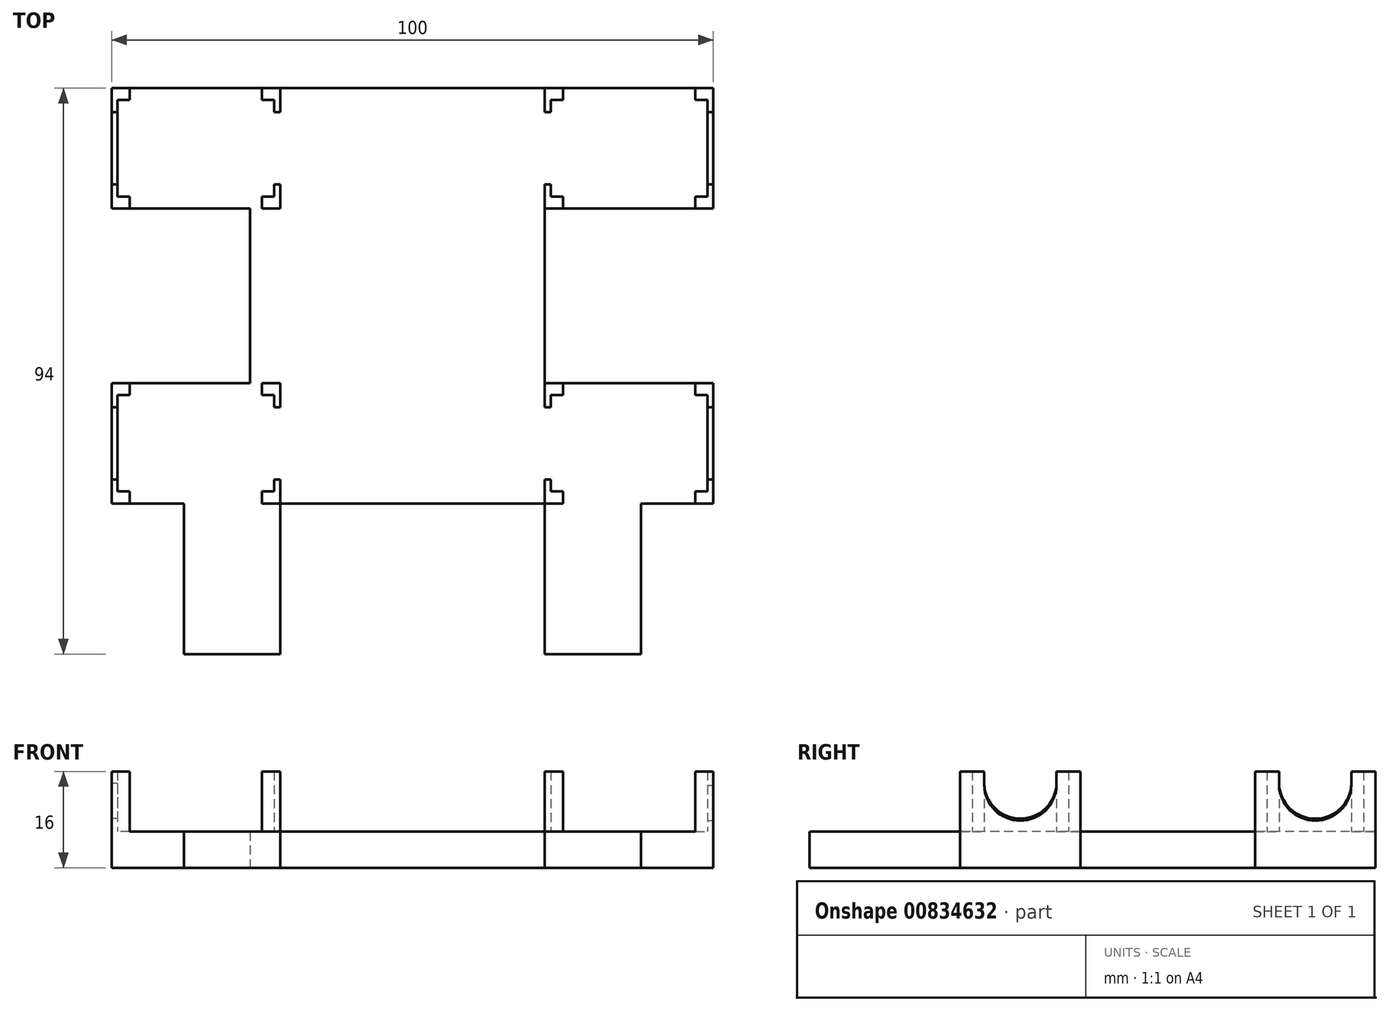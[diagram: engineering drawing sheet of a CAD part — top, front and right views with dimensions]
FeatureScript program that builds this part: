
annotation { "Feature Type Name" : "Feature", "Feature Type Description" : "" }
export const myFeature = defineFeature(function(context is Context, id is Id, definition is map)
    precondition{}
    {
        {
            var Q0;
            Q0=qCreatedBy(makeId("Top.planeOp"),FACE);
            var sketch = newSketch(context, id + "F0", { "sketchPlane" : qUnion([Q0])});
            skLineSegment(sketch, "E0.bottom", {"start": v(-60, -33.28) * mm, "end": v(-44, -33.28) * mm});
            skLineSegment(sketch, "E0.top", {"start": v(-72, 60.72) * mm, "end": v(28, 60.72) * mm});
            skLineSegment(sketch, "E0.right", {"start": v(28, -8.28) * mm, "end": v(28, 11.72) * mm});
            skLineSegment(sketch, "E1.right", {"start": v(-60, -8.28) * mm, "end": v(-60, -33.28) * mm});
            skLineSegment(sketch, "E2.top", {"start": v(-44, -8.28) * mm, "end": v(0, -8.28) * mm});
            skLineSegment(sketch, "E2.left", {"start": v(-44, -33.28) * mm, "end": v(-44, -8.28) * mm});
            skLineSegment(sketch, "E2.right", {"start": v(0, -33.28) * mm, "end": v(0, -8.28) * mm});
            skLineSegment(sketch, "E3.top", {"start": v(16, -8.28) * mm, "end": v(28, -8.28) * mm});
            skLineSegment(sketch, "E3.left", {"start": v(16, -33.28) * mm, "end": v(16, -8.28) * mm});
            skLineSegment(sketch, "E4.top", {"start": v(-72, 40.72) * mm, "end": v(-49, 40.72) * mm});
            skLineSegment(sketch, "E4.right", {"start": v(-49, 11.72) * mm, "end": v(-49, 40.72) * mm});
            skLineSegment(sketch, "E5.bottom", {"start": v(28, 40.72) * mm, "end": v(0, 40.72) * mm});
            skLineSegment(sketch, "E5.top", {"start": v(28, 11.72) * mm, "end": v(0, 11.72) * mm});
            skLineSegment(sketch, "E5.right", {"start": v(0, 40.72) * mm, "end": v(0, 11.72) * mm});
            skLineSegment(sketch, "E6.trimOffspring", {"start": v(28, 40.72) * mm, "end": v(28, 60.72) * mm});
            skLineSegment(sketch, "E7.trimOffspring", {"start": v(0, -33.28) * mm, "end": v(16, -33.28) * mm});
            skLineSegment(sketch, "E8", {"start": v(-72, -8.28) * mm, "end": v(-60, -8.28) * mm});
            skLineSegment(sketch, "E9.left", {"start": v(-72, -8.28) * mm, "end": v(-72, -4.28) * mm});
            skLineSegment(sketch, "E10", {"start": v(-72, -8.28) * mm, "end": v(-69, -8.28) * mm});
            skLineSegment(sketch, "E11", {"start": v(-72, -8.28) * mm, "end": v(-72, 11.74) * mm});
            skLineSegment(sketch, "E12", {"start": v(-72, 11.74) * mm, "end": v(-49, 11.72) * mm});
            skLineSegment(sketch, "E13", {"start": v(-72, 11.7) * mm, "end": v(-69, 11.7) * mm});
            skLineSegment(sketch, "E14.MirrorCS", {"start": v(-72, 11.7) * mm, "end": v(-72, 7.7) * mm});
            skLineSegment(sketch, "E15", {"start": v(-72, 60.72) * mm, "end": v(-72, 40.72) * mm});
            skSolve(sketch);
        }
        {
            var Q0;
            Q0=makeQuery(id+"F0.imprint","IMPRINT",FACE,{"disambiguationData":[TD([[makeQuery(id+"F0.imprint","IMPRINT",EDGE,{"derivedFrom":sQuery(id+"F0.wireOp",EDGE,"E0.bottom")}),1.0]])]});
            extrude(context, id + "F1", {"entities" : qUnion([Q0]), "depth" : 6 * mm, "offsetDistance" : 25 * mm});
        }
        {
            var Q0;
            Q0=makeQuery(id+"F1.opExtrude","CAP_FACE",FACE,{"disambiguationData":[OSD([sQuery(id+"F0.wireOp",EDGE,"E0.bottom"),sQuery(id+"F0.wireOp",EDGE,"E0.top"),sQuery(id+"F0.wireOp",EDGE,"E0.right"),sQuery(id+"F0.wireOp",EDGE,"E1.right"),sQuery(id+"F0.wireOp",EDGE,"E2.top"),sQuery(id+"F0.wireOp",EDGE,"E2.left"),sQuery(id+"F0.wireOp",EDGE,"E2.right"),sQuery(id+"F0.wireOp",EDGE,"E3.top"),sQuery(id+"F0.wireOp",EDGE,"E3.left"),sQuery(id+"F0.wireOp",EDGE,"E4.top"),sQuery(id+"F0.wireOp",EDGE,"E4.right"),sQuery(id+"F0.wireOp",EDGE,"E5.bottom"),sQuery(id+"F0.wireOp",EDGE,"E5.top"),sQuery(id+"F0.wireOp",EDGE,"E5.right"),sQuery(id+"F0.wireOp",EDGE,"E6.trimOffspring"),sQuery(id+"F0.wireOp",EDGE,"E7.trimOffspring"),sQuery(id+"F0.wireOp",EDGE,"E8"),sQuery(id+"F0.wireOp",EDGE,"E10"),sQuery(id+"F0.wireOp",EDGE,"E11"),sQuery(id+"F0.wireOp",EDGE,"E12"),sQuery(id+"F0.wireOp",EDGE,"E14.MirrorCS"),sQuery(id+"F0.wireOp",EDGE,"E15")])],"isStart":false});
            var sketch = newSketch(context, id + "F2", { "sketchPlane" : qUnion([Q0])});
            skLineSegment(sketch, "E16", {"start": v(-72, -8.28) * mm, "end": v(-69, -8.28) * mm});
            skLineSegment(sketch, "E17", {"start": v(-69, -8.28) * mm, "end": v(-69, -6.28) * mm});
            skLineSegment(sketch, "E18", {"start": v(-69, -6.28) * mm, "end": v(-71, -6.28) * mm});
            skLineSegment(sketch, "E19", {"start": v(-71, -6.28) * mm, "end": v(-71, -4.28) * mm});
            skLineSegment(sketch, "E20", {"start": v(-71, -4.28) * mm, "end": v(-72, -4.28) * mm});
            skLineSegment(sketch, "E21", {"start": v(-72, -4.28) * mm, "end": v(-72, -8.28) * mm});
            skLineSegment(sketch, "E22", {"start": v(-72, 1.73) * mm, "end": v(28, 1.73) * mm, "construction": true});
            skLineSegment(sketch, "E23", {"start": v(28, 40.72) * mm, "end": v(28, 11.72) * mm, "construction": true});
            skLineSegment(sketch, "E24", {"start": v(-72, 40.72) * mm, "end": v(-72, 11.74) * mm, "construction": true});
            skLineSegment(sketch, "E25", {"start": v(-22, -8.28) * mm, "end": v(-22, 60.72) * mm, "construction": true});
            skLineSegment(sketch, "E26", {"start": v(-72, 26.23) * mm, "end": v(28, 26.23) * mm, "construction": true});
            skLineSegment(sketch, "E27.MirrorCS", {"start": v(-71, 7.74) * mm, "end": v(-72, 7.74) * mm});
            skLineSegment(sketch, "E28.MirrorCS", {"start": v(-69, 9.74) * mm, "end": v(-71, 9.74) * mm});
            skLineSegment(sketch, "E29.MirrorCS", {"start": v(-69, 11.74) * mm, "end": v(-69, 9.74) * mm});
            skLineSegment(sketch, "E30.MirrorCS", {"start": v(-71, 9.74) * mm, "end": v(-71, 7.74) * mm});
            skLineSegment(sketch, "E31.MirrorCS", {"start": v(-72, 7.74) * mm, "end": v(-72, 11.74) * mm});
            skLineSegment(sketch, "E32.MirrorCS", {"start": v(-72, 11.74) * mm, "end": v(-69, 11.74) * mm});
            skLineSegment(sketch, "E33", {"start": v(-72, 1.73) * mm, "end": v(-57.98, 1.73) * mm});
            skLineSegment(sketch, "E34", {"start": v(-72, 16.41) * mm, "end": v(-58, 16.41) * mm, "construction": true});
            skLineSegment(sketch, "E35", {"start": v(-58, 16.41) * mm, "end": v(-58, -8.8) * mm, "construction": true});
            skLineSegment(sketch, "E36.MirrorCS", {"start": v(-44, 7.74) * mm, "end": v(-44, 11.74) * mm});
            skLineSegment(sketch, "E37.MirrorCS", {"start": v(-45, -4.28) * mm, "end": v(-44, -4.28) * mm});
            skLineSegment(sketch, "E38.MirrorCS", {"start": v(-47, 11.74) * mm, "end": v(-47, 9.74) * mm});
            skLineSegment(sketch, "E39.MirrorCS", {"start": v(-45, 7.74) * mm, "end": v(-44, 7.74) * mm});
            skLineSegment(sketch, "E40.MirrorCS", {"start": v(-47, -6.28) * mm, "end": v(-45, -6.28) * mm});
            skLineSegment(sketch, "E41.MirrorCS", {"start": v(-47, -8.28) * mm, "end": v(-47, -6.28) * mm});
            skLineSegment(sketch, "E42.MirrorCS", {"start": v(-45, -6.28) * mm, "end": v(-45, -4.28) * mm});
            skLineSegment(sketch, "E43.MirrorCS", {"start": v(-47, 9.74) * mm, "end": v(-45, 9.74) * mm});
            skLineSegment(sketch, "E44.MirrorCS", {"start": v(-45, 9.74) * mm, "end": v(-45, 7.74) * mm});
            skLineSegment(sketch, "E45.MirrorCS", {"start": v(-44, -8.28) * mm, "end": v(-47, -8.28) * mm});
            skLineSegment(sketch, "E46.MirrorCS", {"start": v(-44, -4.28) * mm, "end": v(-44, -8.28) * mm});
            skLineSegment(sketch, "E47.MirrorCS", {"start": v(-44, 11.74) * mm, "end": v(-47, 11.74) * mm});
            skLineSegment(sketch, "E48.MirrorCS", {"start": v(27, 7.74) * mm, "end": v(28, 7.74) * mm});
            skLineSegment(sketch, "E49.MirrorCS", {"start": v(27, 9.74) * mm, "end": v(27, 7.74) * mm});
            skLineSegment(sketch, "E50.MirrorCS", {"start": v(28, 7.74) * mm, "end": v(28, 11.74) * mm});
            skLineSegment(sketch, "E51.MirrorCS", {"start": v(25, 11.74) * mm, "end": v(25, 9.74) * mm});
            skLineSegment(sketch, "E52.MirrorCS", {"start": v(1, 9.74) * mm, "end": v(1, 7.74) * mm});
            skLineSegment(sketch, "E53.MirrorCS", {"start": v(25, 9.74) * mm, "end": v(27, 9.74) * mm});
            skLineSegment(sketch, "E54.MirrorCS", {"start": v(3, -6.28) * mm, "end": v(1, -6.28) * mm});
            skLineSegment(sketch, "E55.MirrorCS", {"start": v(3, 9.74) * mm, "end": v(1, 9.74) * mm});
            skLineSegment(sketch, "E56.MirrorCS", {"start": v(1, -6.28) * mm, "end": v(1, -4.28) * mm});
            skLineSegment(sketch, "E57.MirrorCS", {"start": v(3, -8.28) * mm, "end": v(3, -6.28) * mm});
            skLineSegment(sketch, "E58.MirrorCS", {"start": v(1, 7.74) * mm, "end": v(0, 7.74) * mm});
            skLineSegment(sketch, "E59.MirrorCS", {"start": v(25, -8.28) * mm, "end": v(25, -6.28) * mm});
            skLineSegment(sketch, "E60.MirrorCS", {"start": v(25, -6.28) * mm, "end": v(27, -6.28) * mm});
            skLineSegment(sketch, "E61.MirrorCS", {"start": v(27, -6.28) * mm, "end": v(27, -4.28) * mm});
            skLineSegment(sketch, "E62.MirrorCS", {"start": v(0, 7.74) * mm, "end": v(0, 11.74) * mm});
            skLineSegment(sketch, "E63.MirrorCS", {"start": v(27, -4.28) * mm, "end": v(28, -4.28) * mm});
            skLineSegment(sketch, "E64.MirrorCS", {"start": v(3, 11.74) * mm, "end": v(3, 9.74) * mm});
            skLineSegment(sketch, "E65.MirrorCS", {"start": v(1, -4.28) * mm, "end": v(0, -4.28) * mm});
            skLineSegment(sketch, "E66.MirrorCS", {"start": v(28, -8.28) * mm, "end": v(25, -8.28) * mm});
            skLineSegment(sketch, "E67.MirrorCS", {"start": v(28, -4.28) * mm, "end": v(28, -8.28) * mm});
            skLineSegment(sketch, "E68.MirrorCS", {"start": v(0, 11.74) * mm, "end": v(3, 11.74) * mm});
            skLineSegment(sketch, "E69.MirrorCS", {"start": v(0, -4.28) * mm, "end": v(0, -8.28) * mm});
            skLineSegment(sketch, "E70.MirrorCS", {"start": v(0, -8.28) * mm, "end": v(3, -8.28) * mm});
            skLineSegment(sketch, "E71.MirrorCS", {"start": v(28, 11.74) * mm, "end": v(25, 11.74) * mm});
            skLineSegment(sketch, "E72.MirrorCS", {"start": v(28, 1.73) * mm, "end": v(13.98, 1.73) * mm});
            skLineSegment(sketch, "E73.MirrorCS", {"start": v(28, 56.74) * mm, "end": v(28, 60.74) * mm});
            skLineSegment(sketch, "E74.MirrorCS", {"start": v(-71, 58.74) * mm, "end": v(-71, 56.74) * mm});
            skLineSegment(sketch, "E75.MirrorCS", {"start": v(-47, 58.74) * mm, "end": v(-45, 58.74) * mm});
            skLineSegment(sketch, "E76.MirrorCS", {"start": v(-69, 42.72) * mm, "end": v(-71, 42.72) * mm});
            skLineSegment(sketch, "E77.MirrorCS", {"start": v(25, 58.74) * mm, "end": v(27, 58.74) * mm});
            skLineSegment(sketch, "E78.MirrorCS", {"start": v(-47, 42.72) * mm, "end": v(-45, 42.72) * mm});
            skLineSegment(sketch, "E79.MirrorCS", {"start": v(-72, 44.72) * mm, "end": v(-72, 40.72) * mm});
            skLineSegment(sketch, "E80.MirrorCS", {"start": v(27, 58.74) * mm, "end": v(27, 56.74) * mm});
            skLineSegment(sketch, "E81.MirrorCS", {"start": v(-71, 42.72) * mm, "end": v(-71, 44.72) * mm});
            skLineSegment(sketch, "E82.MirrorCS", {"start": v(-45, 58.74) * mm, "end": v(-45, 56.74) * mm});
            skLineSegment(sketch, "E83.MirrorCS", {"start": v(-45, 42.72) * mm, "end": v(-45, 44.72) * mm});
            skLineSegment(sketch, "E84.MirrorCS", {"start": v(-44, 56.74) * mm, "end": v(-44, 60.74) * mm});
            skLineSegment(sketch, "E85.MirrorCS", {"start": v(-69, 58.74) * mm, "end": v(-71, 58.74) * mm});
            skLineSegment(sketch, "E86.MirrorCS", {"start": v(-72, 40.72) * mm, "end": v(-69, 40.72) * mm});
            skLineSegment(sketch, "E87.MirrorCS", {"start": v(27, 44.72) * mm, "end": v(28, 44.72) * mm});
            skLineSegment(sketch, "E88.MirrorCS", {"start": v(3, 40.72) * mm, "end": v(3, 42.72) * mm});
            skLineSegment(sketch, "E89.MirrorCS", {"start": v(27, 42.72) * mm, "end": v(27, 44.72) * mm});
            skLineSegment(sketch, "E90.MirrorCS", {"start": v(1, 56.74) * mm, "end": v(0, 56.74) * mm});
            skLineSegment(sketch, "E91.MirrorCS", {"start": v(-72, 56.74) * mm, "end": v(-72, 60.74) * mm});
            skLineSegment(sketch, "E92.MirrorCS", {"start": v(28, 44.72) * mm, "end": v(28, 40.72) * mm});
            skLineSegment(sketch, "E93.MirrorCS", {"start": v(28, 60.74) * mm, "end": v(25, 60.74) * mm});
            skLineSegment(sketch, "E94.MirrorCS", {"start": v(-71, 56.74) * mm, "end": v(-72, 56.74) * mm});
            skLineSegment(sketch, "E95.MirrorCS", {"start": v(25, 40.72) * mm, "end": v(25, 42.72) * mm});
            skLineSegment(sketch, "E96.MirrorCS", {"start": v(-44, 40.72) * mm, "end": v(-47, 40.72) * mm});
            skLineSegment(sketch, "E97.MirrorCS", {"start": v(27, 56.74) * mm, "end": v(28, 56.74) * mm});
            skLineSegment(sketch, "E98.MirrorCS", {"start": v(-44, 44.72) * mm, "end": v(-44, 40.72) * mm});
            skLineSegment(sketch, "E99.MirrorCS", {"start": v(-44, 60.74) * mm, "end": v(-47, 60.74) * mm});
            skLineSegment(sketch, "E100.MirrorCS", {"start": v(3, 42.72) * mm, "end": v(1, 42.72) * mm});
            skLineSegment(sketch, "E101.MirrorCS", {"start": v(3, 58.74) * mm, "end": v(1, 58.74) * mm});
            skLineSegment(sketch, "E102.MirrorCS", {"start": v(3, 60.74) * mm, "end": v(3, 58.74) * mm});
            skLineSegment(sketch, "E103.MirrorCS", {"start": v(28, 40.72) * mm, "end": v(25, 40.72) * mm});
            skLineSegment(sketch, "E104.MirrorCS", {"start": v(-69, 60.74) * mm, "end": v(-69, 58.74) * mm});
            skLineSegment(sketch, "E105.MirrorCS", {"start": v(0, 60.74) * mm, "end": v(3, 60.74) * mm});
            skLineSegment(sketch, "E106.MirrorCS", {"start": v(-71, 44.72) * mm, "end": v(-72, 44.72) * mm});
            skLineSegment(sketch, "E107.MirrorCS", {"start": v(-45, 56.74) * mm, "end": v(-44, 56.74) * mm});
            skLineSegment(sketch, "E108.MirrorCS", {"start": v(1, 44.72) * mm, "end": v(0, 44.72) * mm});
            skLineSegment(sketch, "E109.MirrorCS", {"start": v(-47, 60.74) * mm, "end": v(-47, 58.74) * mm});
            skLineSegment(sketch, "E110.MirrorCS", {"start": v(0, 56.74) * mm, "end": v(0, 60.74) * mm});
            skLineSegment(sketch, "E111.MirrorCS", {"start": v(0, 40.72) * mm, "end": v(3, 40.72) * mm});
            skLineSegment(sketch, "E112.MirrorCS", {"start": v(0, 44.72) * mm, "end": v(0, 40.72) * mm});
            skLineSegment(sketch, "E113.MirrorCS", {"start": v(-47, 40.72) * mm, "end": v(-47, 42.72) * mm});
            skLineSegment(sketch, "E114.MirrorCS", {"start": v(1, 42.72) * mm, "end": v(1, 44.72) * mm});
            skLineSegment(sketch, "E115.MirrorCS", {"start": v(25, 60.74) * mm, "end": v(25, 58.74) * mm});
            skLineSegment(sketch, "E116.MirrorCS", {"start": v(25, 42.72) * mm, "end": v(27, 42.72) * mm});
            skLineSegment(sketch, "E117.MirrorCS", {"start": v(-72, 60.74) * mm, "end": v(-69, 60.74) * mm});
            skLineSegment(sketch, "E118.MirrorCS", {"start": v(-45, 44.72) * mm, "end": v(-44, 44.72) * mm});
            skLineSegment(sketch, "E119.MirrorCS", {"start": v(-69, 40.72) * mm, "end": v(-69, 42.72) * mm});
            skLineSegment(sketch, "E120.MirrorCS", {"start": v(1, 58.74) * mm, "end": v(1, 56.74) * mm});
            skLineSegment(sketch, "E121.MirrorCS", {"start": v(-72, 50.73) * mm, "end": v(-57.98, 50.73) * mm});
            skLineSegment(sketch, "E122.MirrorCS", {"start": v(28, 50.73) * mm, "end": v(13.98, 50.73) * mm});
            skLineSegment(sketch, "E123.MirrorCS", {"start": v(-72, 50.73) * mm, "end": v(28, 50.73) * mm, "construction": true});
            skSolve(sketch);
        }
        {
            var Q0;
            Q0=makeQuery(id+"F2.imprint","IMPRINT",FACE,{"disambiguationData":[TD([[makeQuery(id+"F2.imprint","IMPRINT",EDGE,{"derivedFrom":sQuery(id+"F2.wireOp",EDGE,"E74.MirrorCS")}),-1.0]])]});
            var Q1;
            Q1=makeQuery(id+"F2.imprint","IMPRINT",FACE,{"disambiguationData":[TD([[makeQuery(id+"F2.imprint","IMPRINT",EDGE,{"derivedFrom":sQuery(id+"F2.wireOp",EDGE,"E76.MirrorCS")}),1.0]])]});
            var Q2;
            Q2=makeQuery(id+"F2.imprint","IMPRINT",FACE,{"disambiguationData":[TD([[makeQuery(id+"F2.imprint","IMPRINT",EDGE,{"derivedFrom":sQuery(id+"F2.wireOp",EDGE,"E78.MirrorCS")}),-1.0]])]});
            var Q3;
            {var subQ6=sQuery(id+"F2.wireOp",EDGE,"E75.MirrorCS");Q3=makeQuery(id+"F2.imprint","IMPRINT",FACE,{"disambiguationData":[TD([[makeQuery(id+"F2.imprint","IMPRINT",EDGE,{"derivedFrom":subQ6}),1.0]])]});}
            var Q4;
            {var subQ1=sQuery(id+"F2.wireOp",EDGE,"E77.MirrorCS");Q4=makeQuery(id+"F2.imprint","IMPRINT",FACE,{"disambiguationData":[TD([[makeQuery(id+"F2.imprint","IMPRINT",EDGE,{"derivedFrom":subQ1}),1.0]])]});}
            var Q5;
            Q5=makeQuery(id+"F2.imprint","IMPRINT",FACE,{"disambiguationData":[TD([[makeQuery(id+"F2.imprint","IMPRINT",EDGE,{"derivedFrom":sQuery(id+"F2.wireOp",EDGE,"E87.MirrorCS")}),-1.0]])]});
            var Q6;
            Q6=makeQuery(id+"F2.imprint","IMPRINT",FACE,{"disambiguationData":[TD([[makeQuery(id+"F2.imprint","IMPRINT",EDGE,{"derivedFrom":sQuery(id+"F2.wireOp",EDGE,"E88.MirrorCS")}),1.0]])]});
            var Q7;
            {var subQ1=sQuery(id+"F2.wireOp",EDGE,"E90.MirrorCS");Q7=makeQuery(id+"F2.imprint","IMPRINT",FACE,{"disambiguationData":[TD([[makeQuery(id+"F2.imprint","IMPRINT",EDGE,{"derivedFrom":subQ1}),-1.0]])]});}
            var Q8;
            {var subQ3=sQuery(id+"F2.wireOp",EDGE,"E48.MirrorCS");Q8=makeQuery(id+"F2.imprint","IMPRINT",FACE,{"disambiguationData":[TD([[makeQuery(id+"F2.imprint","IMPRINT",EDGE,{"derivedFrom":subQ3}),1.0]])]});}
            var Q9;
            Q9=makeQuery(id+"F2.imprint","IMPRINT",FACE,{"disambiguationData":[TD([[makeQuery(id+"F2.imprint","IMPRINT",EDGE,{"derivedFrom":sQuery(id+"F2.wireOp",EDGE,"E59.MirrorCS")}),-1.0]])]});
            var Q10;
            Q10=makeQuery(id+"F2.imprint","IMPRINT",FACE,{"disambiguationData":[TD([[makeQuery(id+"F2.imprint","IMPRINT",EDGE,{"derivedFrom":sQuery(id+"F2.wireOp",EDGE,"E54.MirrorCS")}),1.0]])]});
            var Q11;
            Q11=makeQuery(id+"F2.imprint","IMPRINT",FACE,{"disambiguationData":[TD([[makeQuery(id+"F2.imprint","IMPRINT",EDGE,{"derivedFrom":sQuery(id+"F2.wireOp",EDGE,"E52.MirrorCS")}),-1.0]])]});
            var Q12;
            Q12=makeQuery(id+"F2.imprint","IMPRINT",FACE,{"disambiguationData":[TD([[makeQuery(id+"F2.imprint","IMPRINT",EDGE,{"derivedFrom":sQuery(id+"F2.wireOp",EDGE,"E36.MirrorCS")}),1.0]])]});
            var Q13;
            Q13=makeQuery(id+"F2.imprint","IMPRINT",FACE,{"disambiguationData":[TD([[makeQuery(id+"F2.imprint","IMPRINT",EDGE,{"derivedFrom":sQuery(id+"F2.wireOp",EDGE,"E37.MirrorCS")}),-1.0]])]});
            var Q14;
            Q14=makeQuery(id+"F2.imprint","IMPRINT",FACE,{"disambiguationData":[TD([[makeQuery(id+"F2.imprint","IMPRINT",EDGE,{"derivedFrom":sQuery(id+"F2.wireOp",EDGE,"E16")}),1.0]])]});
            var Q15;
            Q15=makeQuery(id+"F2.imprint","IMPRINT",FACE,{"disambiguationData":[TD([[makeQuery(id+"F2.imprint","IMPRINT",EDGE,{"derivedFrom":sQuery(id+"F2.wireOp",EDGE,"E27.MirrorCS")}),-1.0]])]});
            extrude(context, id + "F3", {"entities" : qUnion([Q0, Q1, Q2, Q3, Q4, Q5, Q6, Q7, Q8, Q9, Q10, Q11, Q12, Q13, Q14, Q15]), "operationType" : NewBodyOperationType.ADD, "depth" : 10 * mm, "offsetDistance" : 25 * mm});
        }
        {
            var Q0;
            Q0=makeQuery(id+"F3.boolean.opBoolean","MERGE",FACE,{"derivedFrom":[makeQuery(id+"F1.opExtrude","SWEPT_FACE",FACE,{"disambiguationData":[OSD([sQuery(id+"F0.wireOp",EDGE,"E0.right")])]}),makeQuery(id+"F3.opExtrude","SWEPT_FACE",FACE,{"disambiguationData":[OSD([sQuery(id+"F2.wireOp",EDGE,"E50.MirrorCS")])]}),makeQuery(id+"F3.opExtrude","SWEPT_FACE",FACE,{"disambiguationData":[OSD([sQuery(id+"F2.wireOp",EDGE,"E67.MirrorCS")])]})]});
            var sketch = newSketch(context, id + "F4", { "sketchPlane" : qUnion([Q0])});
            skArc(sketch, "E124", {"start": v(-4.28, 14) * mm, "mid": v(1.73, 7.82) * mm, "end": v(7.74, 14) * mm});
            skSolve(sketch);
        }
        {
            var Q0;
            {var subQ1=sQuery(id+"F0.wireOp",EDGE,"E0.right");var subQ6=makeQuery(id+"F1.opExtrude","CAP_EDGE",EDGE,{"disambiguationData":[OSD([subQ1])],"isStart":false});Q0=makeQuery(id+"F4.imprint","IMPRINT",FACE,{"disambiguationData":[TD([[makeQuery(id+"F4.imprint","IMPRINT",EDGE,{"derivedFrom":subQ6}),1.0]])]});}
            extrude(context, id + "F5", {"entities" : qUnion([Q0]), "operationType" : NewBodyOperationType.ADD, "oppositeDirection" : true, "depth" : 1 * mm, "offsetDistance" : 25 * mm});
        }
        {
            var Q0;
            Q0=makeQuery(id+"F3.boolean.opBoolean","MERGE",FACE,{"derivedFrom":[makeQuery(id+"F1.opExtrude","SWEPT_FACE",FACE,{"disambiguationData":[OSD([sQuery(id+"F0.wireOp",EDGE,"E6.trimOffspring")])]}),makeQuery(id+"F3.opExtrude","SWEPT_FACE",FACE,{"disambiguationData":[OSD([sQuery(id+"F2.wireOp",EDGE,"E73.MirrorCS")])]}),makeQuery(id+"F3.opExtrude","SWEPT_FACE",FACE,{"disambiguationData":[OSD([sQuery(id+"F2.wireOp",EDGE,"E92.MirrorCS")])]})]});
            var sketch = newSketch(context, id + "F6", { "sketchPlane" : qUnion([Q0])});
            skArc(sketch, "E125", {"start": v(44.72, 14) * mm, "mid": v(50.73, 7.82) * mm, "end": v(56.74, 14) * mm});
            skSolve(sketch);
        }
        {
            var Q0;
            {var subQ1=sQuery(id+"F0.wireOp",EDGE,"E6.trimOffspring");var subQ6=makeQuery(id+"F1.opExtrude","CAP_EDGE",EDGE,{"disambiguationData":[OSD([subQ1])],"isStart":false});Q0=makeQuery(id+"F6.imprint","IMPRINT",FACE,{"disambiguationData":[TD([[makeQuery(id+"F6.imprint","IMPRINT",EDGE,{"derivedFrom":subQ6}),1.0]])]});}
            extrude(context, id + "F7", {"entities" : qUnion([Q0]), "operationType" : NewBodyOperationType.ADD, "oppositeDirection" : true, "depth" : 1 * mm, "offsetDistance" : 25 * mm});
        }
        {
            var Q0;
            Q0=makeQuery(id+"F3.boolean.opBoolean","MERGE",FACE,{"derivedFrom":[makeQuery(id+"F1.opExtrude","SWEPT_FACE",FACE,{"disambiguationData":[OSD([sQuery(id+"F0.wireOp",EDGE,"E15")])]}),makeQuery(id+"F3.opExtrude","SWEPT_FACE",FACE,{"disambiguationData":[OSD([sQuery(id+"F2.wireOp",EDGE,"E79.MirrorCS")])]}),makeQuery(id+"F3.opExtrude","SWEPT_FACE",FACE,{"disambiguationData":[OSD([sQuery(id+"F2.wireOp",EDGE,"E91.MirrorCS")])]})]});
            var sketch = newSketch(context, id + "F8", { "sketchPlane" : qUnion([Q0])});
            skArc(sketch, "E126", {"start": v(-7.74, 14) * mm, "mid": v(-1.73, 7.82) * mm, "end": v(4.28, 14) * mm});
            skArc(sketch, "E127", {"start": v(-56.74, 14) * mm, "mid": v(-50.73, 8.14) * mm, "end": v(-44.72, 14) * mm});
            skLineSegment(sketch, "E128", {"start": v(-7.74, 14) * mm, "end": v(-7.74, 5.95) * mm});
            skLineSegment(sketch, "E129", {"start": v(-7.74, 5.95) * mm, "end": v(4.39, 5.95) * mm});
            skLineSegment(sketch, "E130", {"start": v(4.39, 5.95) * mm, "end": v(4.28, 14) * mm});
            skSolve(sketch);
        }
        {
            var Q0;
            {var subQ0=sQuery(id+"F8.wireOp",EDGE,"E127");Q0=makeQuery(id+"F8.imprint","IMPRINT",FACE,{"disambiguationData":[TD([[makeQuery(id+"F8.imprint","IMPRINT",EDGE,{"derivedFrom":subQ0}),-1.0]])]});}
            extrude(context, id + "F9", {"entities" : qUnion([Q0]), "operationType" : NewBodyOperationType.ADD, "oppositeDirection" : true, "depth" : 1 * mm, "offsetDistance" : 25 * mm});
        }
        {
            var Q0;
            {var subQ5=sQuery(id+"F8.wireOp",EDGE,"E129");Q0=makeQuery(id+"F8.imprint","IMPRINT",FACE,{"disambiguationData":[TD([[makeQuery(id+"F8.imprint","IMPRINT",EDGE,{"derivedFrom":subQ5}),1.0]])]});}
            extrude(context, id + "F10", {"entities" : qUnion([Q0]), "oppositeDirection" : true, "depth" : 1 * mm, "offsetDistance" : 25 * mm});
        }
        {
            var Q0;
            Q0=makeQuery(id+"F10.opExtrude","SWEPT_BODY",BODY,{"disambiguationData":[OSD([sQuery(id+"F8.wireOp",EDGE,"E126"),sQuery(id+"F8.wireOp",EDGE,"E128"),sQuery(id+"F8.wireOp",EDGE,"E129"),sQuery(id+"F8.wireOp",EDGE,"E130")])]});
            deleteBodies(context, id + "F11", {"entities" : qUnion([Q0])});
        }
        {
            var Q0;
            Q0=makeQuery(id+"F3.boolean.opBoolean","MERGE",FACE,{"derivedFrom":[makeQuery(id+"F1.opExtrude","SWEPT_FACE",FACE,{"disambiguationData":[OSD([sQuery(id+"F0.wireOp",EDGE,"E11"),sQuery(id+"F0.wireOp",EDGE,"E14.MirrorCS")])]}),makeQuery(id+"F3.opExtrude","SWEPT_FACE",FACE,{"disambiguationData":[OSD([sQuery(id+"F2.wireOp",EDGE,"E21")])]}),makeQuery(id+"F3.opExtrude","SWEPT_FACE",FACE,{"disambiguationData":[OSD([sQuery(id+"F2.wireOp",EDGE,"E31.MirrorCS")])]})]});
            var sketch = newSketch(context, id + "F12", { "sketchPlane" : qUnion([Q0])});
            skArc(sketch, "E131", {"start": v(-7.74, 14) * mm, "mid": v(-1.73, 8.15) * mm, "end": v(4.28, 14) * mm});
            skSolve(sketch);
        }
        {
            var Q0;
            {var subQ0=sQuery(id+"F12.wireOp",EDGE,"E131");Q0=makeQuery(id+"F12.imprint","IMPRINT",FACE,{"disambiguationData":[TD([[makeQuery(id+"F12.imprint","IMPRINT",EDGE,{"derivedFrom":subQ0}),-1.0]])]});}
            extrude(context, id + "F13", {"entities" : qUnion([Q0]), "operationType" : NewBodyOperationType.ADD, "oppositeDirection" : true, "depth" : 1 * mm, "offsetDistance" : 25 * mm});
        }
    });
